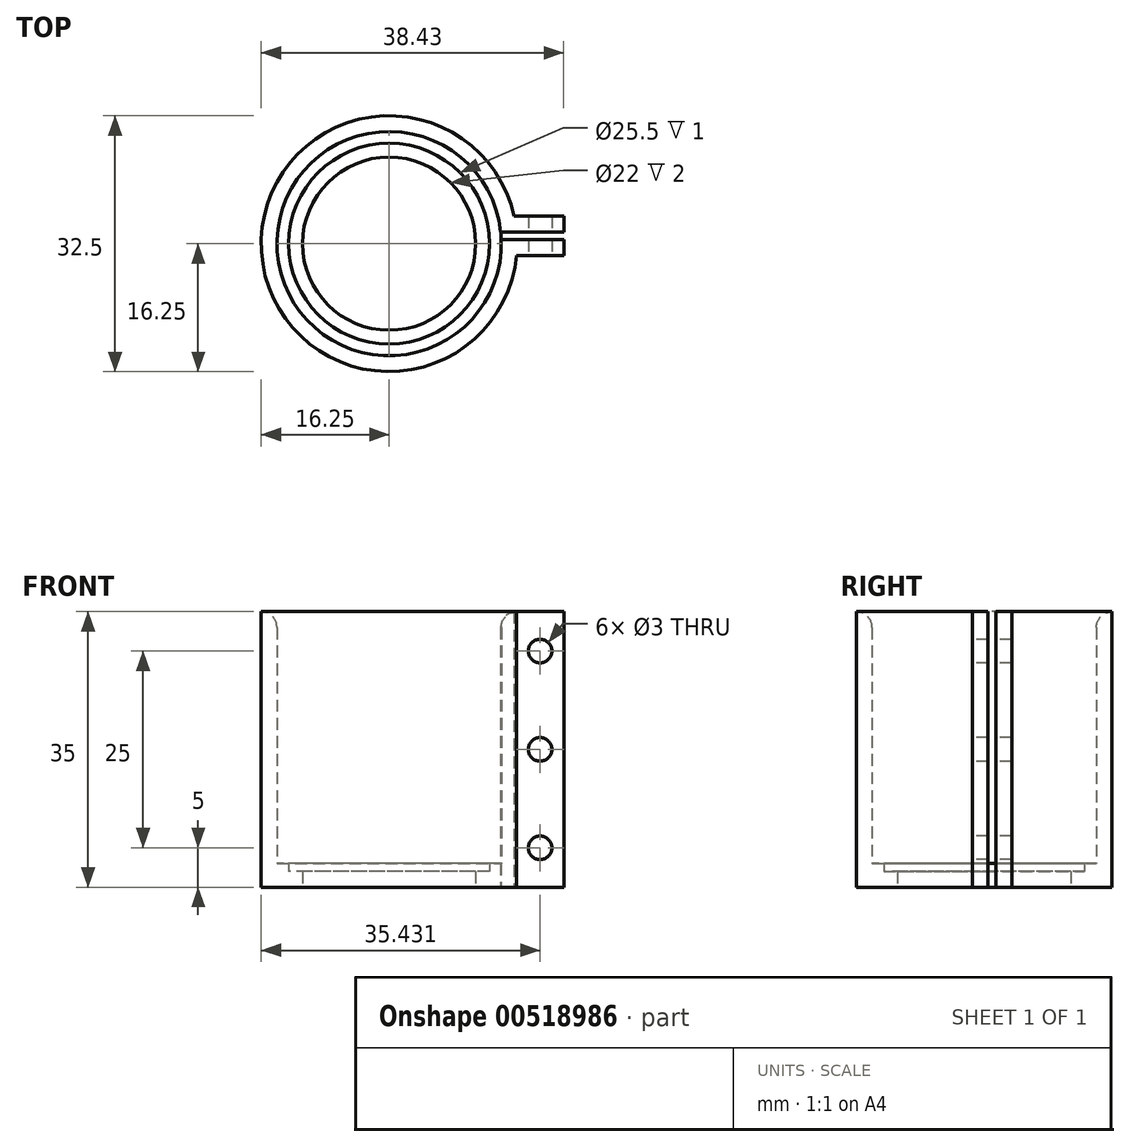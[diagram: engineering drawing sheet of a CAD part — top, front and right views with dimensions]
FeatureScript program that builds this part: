
annotation { "Feature Type Name" : "Feature", "Feature Type Description" : "" }
export const myFeature = defineFeature(function(context is Context, id is Id, definition is map)
    precondition{}
    {
        {
            var Q0;
            Q0=qCreatedBy(makeId("Top.planeOp"),FACE);
            var sketch = newSketch(context, id + "F0", { "sketchPlane" : qUnion([Q0])});
            skCircle(sketch, "E0", {"center": v(0, 0) * mm, "radius": 14.25 * mm});
            skCircle(sketch, "E1", {"center": v(0, 0) * mm, "radius": 16.25 * mm});
            skLineSegment(sketch, "E2", {"start": v(14.17, 1.5) * mm, "end": v(16.18, 1.5) * mm});
            skLineSegment(sketch, "E3", {"start": v(14.24, 0.5) * mm, "end": v(16.18, 0.5) * mm});
            skLineSegment(sketch, "E4", {"start": v(15.87, 3.5) * mm, "end": v(22.18, 3.5) * mm});
            skLineSegment(sketch, "E5", {"start": v(22.18, 3.5) * mm, "end": v(22.18, 1.5) * mm});
            skLineSegment(sketch, "E6", {"start": v(22.18, 1.5) * mm, "end": v(16.18, 1.5) * mm});
            skLineSegment(sketch, "E7", {"start": v(16.18, 0.5) * mm, "end": v(22.18, 0.5) * mm});
            skLineSegment(sketch, "E8", {"start": v(22.18, 0.5) * mm, "end": v(22.18, -1.5) * mm});
            skLineSegment(sketch, "E9", {"start": v(22.18, -1.5) * mm, "end": v(16.18, -1.5) * mm});
            skCircle(sketch, "E10", {"center": v(0, 0) * mm, "radius": 11 * mm});
            skCircle(sketch, "E11", {"center": v(0, 0) * mm, "radius": 12.75 * mm});
            skSolve(sketch);
        }
        {
            var Q0;
            {var subQ0=sQuery(id+"F0.wireOp",EDGE,"E2");Q0=makeQuery(id+"F0.imprint","IMPRINT",FACE,{"disambiguationData":[TD([[makeQuery(id+"F0.imprint","IMPRINT",EDGE,{"derivedFrom":subQ0}),1.0]])]});}
            var Q1;
            {var subQ2=sQuery(id+"F0.wireOp",EDGE,"E4");Q1=makeQuery(id+"F0.imprint","IMPRINT",FACE,{"disambiguationData":[TD([[makeQuery(id+"F0.imprint","IMPRINT",EDGE,{"derivedFrom":subQ2}),-1.0]])]});}
            var Q2;
            {var subQ4=sQuery(id+"F0.wireOp",EDGE,"E8");Q2=makeQuery(id+"F0.imprint","IMPRINT",FACE,{"disambiguationData":[TD([[makeQuery(id+"F0.imprint","IMPRINT",EDGE,{"derivedFrom":subQ4}),-1.0]])]});}
            extrude(context, id + "F1", {"entities" : qUnion([Q0, Q1, Q2]), "depth" : 35 * mm, "offsetDistance" : 25 * mm});
        }
        {
            var Q0;
            Q0=makeQuery(id+"F0.imprint","IMPRINT",FACE,{"disambiguationData":[TD([[makeQuery(id+"F0.imprint","IMPRINT",EDGE,{"derivedFrom":sQuery(id+"F0.wireOp",EDGE,"E11")}),-1.0]])]});
            extrude(context, id + "F2", {"entities" : qUnion([Q0]), "operationType" : NewBodyOperationType.ADD, "depth" : 3 * mm, "offsetDistance" : 25 * mm});
        }
        {
            var Q0;
            Q0=makeQuery(id+"F0.imprint","IMPRINT",FACE,{"disambiguationData":[TD([[makeQuery(id+"F0.imprint","IMPRINT",EDGE,{"derivedFrom":sQuery(id+"F0.wireOp",EDGE,"E10")}),-1.0]])]});
            extrude(context, id + "F3", {"entities" : qUnion([Q0]), "operationType" : NewBodyOperationType.ADD, "depth" : 2 * mm, "offsetDistance" : 25 * mm});
        }
        {
            var Q0;
            Q0=makeQuery(id+"F1.opExtrude","SWEPT_FACE",FACE,{"disambiguationData":[OSD([sQuery(id+"F0.wireOp",EDGE,"E9")])]});
            var sketch = newSketch(context, id + "F4", { "sketchPlane" : qUnion([Q0])});
            skCircle(sketch, "E12", {"center": v(19.18, 30) * mm, "radius": 1.5 * mm});
            skCircle(sketch, "E13", {"center": v(19.18, 5) * mm, "radius": 1.5 * mm});
            skCircle(sketch, "E14", {"center": v(19.18, 17.5) * mm, "radius": 1.5 * mm});
            skLineSegment(sketch, "E15", {"start": v(19.18, 30) * mm, "end": v(19.18, 35) * mm, "construction": true});
            skLineSegment(sketch, "E16", {"start": v(19.18, 5) * mm, "end": v(19.18, 0) * mm, "construction": true});
            skLineSegment(sketch, "E17", {"start": v(19.18, 30) * mm, "end": v(19.18, 17.5) * mm, "construction": true});
            skLineSegment(sketch, "E18", {"start": v(19.18, 17.5) * mm, "end": v(19.18, 5) * mm, "construction": true});
            skLineSegment(sketch, "E19", {"start": v(19.18, 5) * mm, "end": v(22.18, 5) * mm, "construction": true});
            skSolve(sketch);
        }
        {
            var Q0;
            Q0 = qSketchRegion(id + "F4", true);
            extrude(context, id + "F5", {"entities" : qUnion([Q0]), "operationType" : NewBodyOperationType.REMOVE, "oppositeDirection" : true, "depth" : 25 * mm, "offsetDistance" : 25 * mm});
        }
        {
            var Q0;
            Q0=makeQuery(id+"F1.opExtrude","CAP_EDGE",EDGE,{"disambiguationData":[OSD([sQuery(id+"F0.wireOp",EDGE,"E0")])],"isStart":false});
            fillet(context, id + "F6", {"entities" : qUnion([Q0]), "radius" : 2 * mm, "tangentPropagation" : true, "allowEdgeOverflow" : false});
        }
    });
